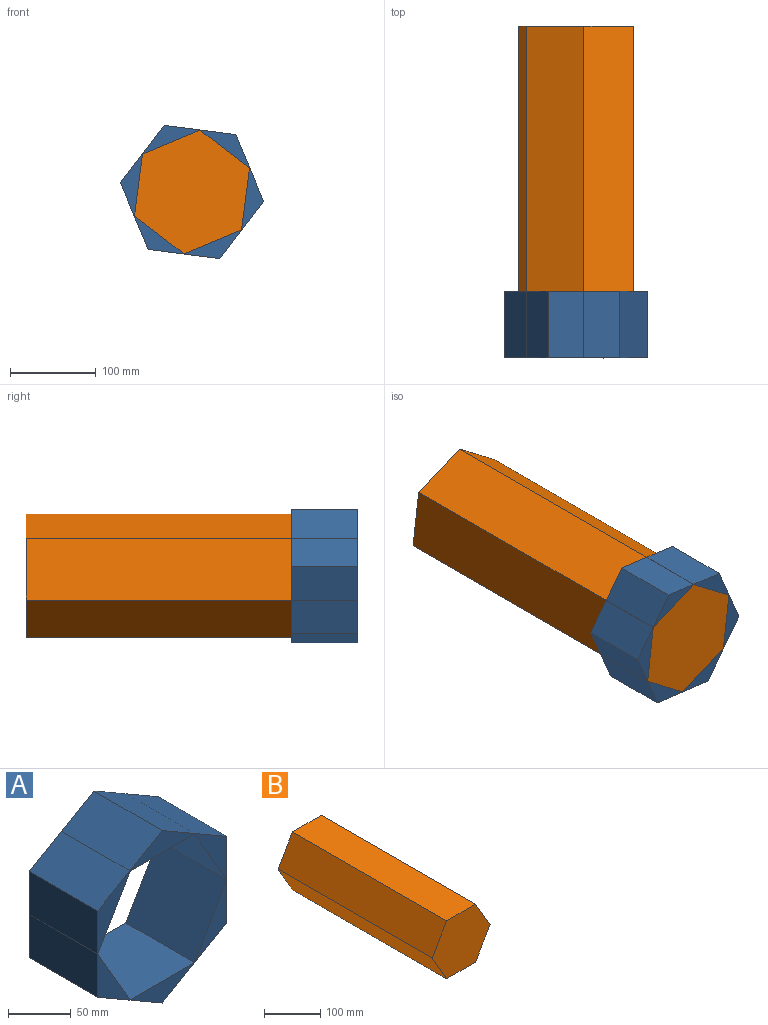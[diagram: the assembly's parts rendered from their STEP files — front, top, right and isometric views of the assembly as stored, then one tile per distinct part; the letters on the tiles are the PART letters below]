
ASSEMBLY  parts=2 mates=1
PART A: 14 faces, bbox 145.5x77.2x168 mm
  f0: plane 84.02x77.25mm, normal (1,0,0), area 6490.1mm2, adj f1,f2,f3,f7
  f1: plane 77.25x72.76mm, normal (0.5,0,-0.87), area 6490.1mm2, adj f0,f2,f3,f4
  f2: plane 168.03x145.52mm, normal (0,-1,0), area 4695.5mm2, adj f0,f1,f4,f5,f6,f7,f8,f9
  f3: plane 168.03x145.52mm, normal (0,1,0), area 4695.5mm2, adj f0,f1,f4,f5,f6,f7,f8,f9
  f4: plane 77.25x72.76mm, normal (-0.5,0,-0.87), area 6490.1mm2, adj f1,f2,f3,f5
  f5: plane 84.02x77.25mm, normal (-1,0,0), area 6490.1mm2, adj f2,f3,f4,f6
  f6: plane 77.25x72.76mm, normal (-0.5,0,0.87), area 6490.1mm2, adj f2,f3,f5,f7
  f7: plane 77.25x72.76mm, normal (0.5,0,0.87), area 6490.1mm2, adj f0,f2,f3,f6
  f8: plane 77.25x62.76mm, normal (-0.87,0,0.5), area 5598mm2, adj f2,f3,f9,f10
  f9: plane 77.25x72.47mm, normal (0,0,1), area 5598mm2, adj f2,f3,f8,f11
  f10: plane 77.25x62.76mm, normal (-0.87,0,-0.5), area 5598mm2, adj f2,f3,f8,f13
  f11: plane 77.25x62.76mm, normal (0.87,0,0.5), area 5598mm2, adj f2,f3,f9,f12
  f12: plane 77.25x62.76mm, normal (0.87,0,-0.5), area 5598mm2, adj f2,f3,f11,f13
  f13: plane 77.25x72.47mm, normal (0,0,-1), area 5598mm2, adj f2,f3,f10,f12
PART B: 8 faces, bbox 144.9x386x125.5 mm
  f0: plane 385.97x62.76mm, normal (0.87,0,0.5), area 27970.5mm2, adj f1,f5,f6,f7
  f1: plane 385.97x72.47mm, normal (0,0,1), area 27970.5mm2, adj f0,f2,f6,f7
  f2: plane 385.97x62.76mm, normal (-0.87,0,0.5), area 27970.5mm2, adj f1,f3,f6,f7
  f3: plane 385.97x62.76mm, normal (-0.87,0,-0.5), area 27970.5mm2, adj f2,f4,f6,f7
  f4: plane 385.97x72.47mm, normal (0,0,-1), area 27970.5mm2, adj f3,f5,f6,f7
  f5: plane 385.97x62.76mm, normal (0.87,0,-0.5), area 27970.5mm2, adj f0,f4,f6,f7
  f6: plane 144.94x125.52mm, normal (0,-1,0), area 13643.9mm2, adj f0,f1,f2,f3,f4,f5
  f7: plane 144.94x125.52mm, normal (0,1,0), area 13643.9mm2, adj f0,f1,f2,f3,f4,f5
PLACE A rot(axis=(0.75,0,0.66),180deg) t=(-145.67,429.32,-31.84)mm
PLACE B rot(axis=(0,1,0),97.3deg) t=(-145.67,699.56,-31.84)mm
MATE slider A.f3 <-> B.f6  axis (0,-1,0) through (-145.67,429.32,-31.84)mm
